# Revit family: DA_Клапан_Регулятор_VAV- РРДР_VEOX
name_source: partatom
category: Арматура воздуховодов
units: mm (PartAtom-declared; Revit-internal decimal feet)

## family parameters
Всегда вертикально = Нет
На основе рабочей плоскости = Нет
Номер OmniClass = 23.33.41.17.13
Общий = Нет
При загрузке вырезать с полостями = Нет
Размер круглого соединителя = Использовать диаметр
Тип детали = Вставляется

## types (4) — shared parameters
ADSK_Дата изменения = 26.12.2022
ADSK_Завод-изготовитель = Veox
ADSK_Количество = 1
ADSK_Напряжение = 24 В
CSV = VAV
URL = https://veox.ru
КМС = 0.7
Корпус = Оцинкованная сталь
Лопатка = Оцинкованная сталь
Максимальный размер клапана = 400мм
Минимальный размер клапана = 100мм
Фланец = Оцинкованная сталь
zero-valued in all types: Отметка по умолчанию

## per-type parameters (varying)
| type | ADSK_Единица измерения | ADSK_Наименование краткое | ИЗОЛЯЦИЯ | сдвиг изоляции | тип |
| РРДР DN100-400  Belimo (с изоляцией) | шт. | РРДР | Да | 50 мм | 11 |
| РРДР DN100-400  Belimo (без изоляции) | шт |  | Нет | 0 мм | 1 |
| РРДР DN100-400 Gruner (без изоляции) | шт. |  | Нет | 0 мм | 2 |
| РРДР DN100-400 Gruner (с изоляцией) | шт. | РРДР | Да | 50 мм | 22 |
